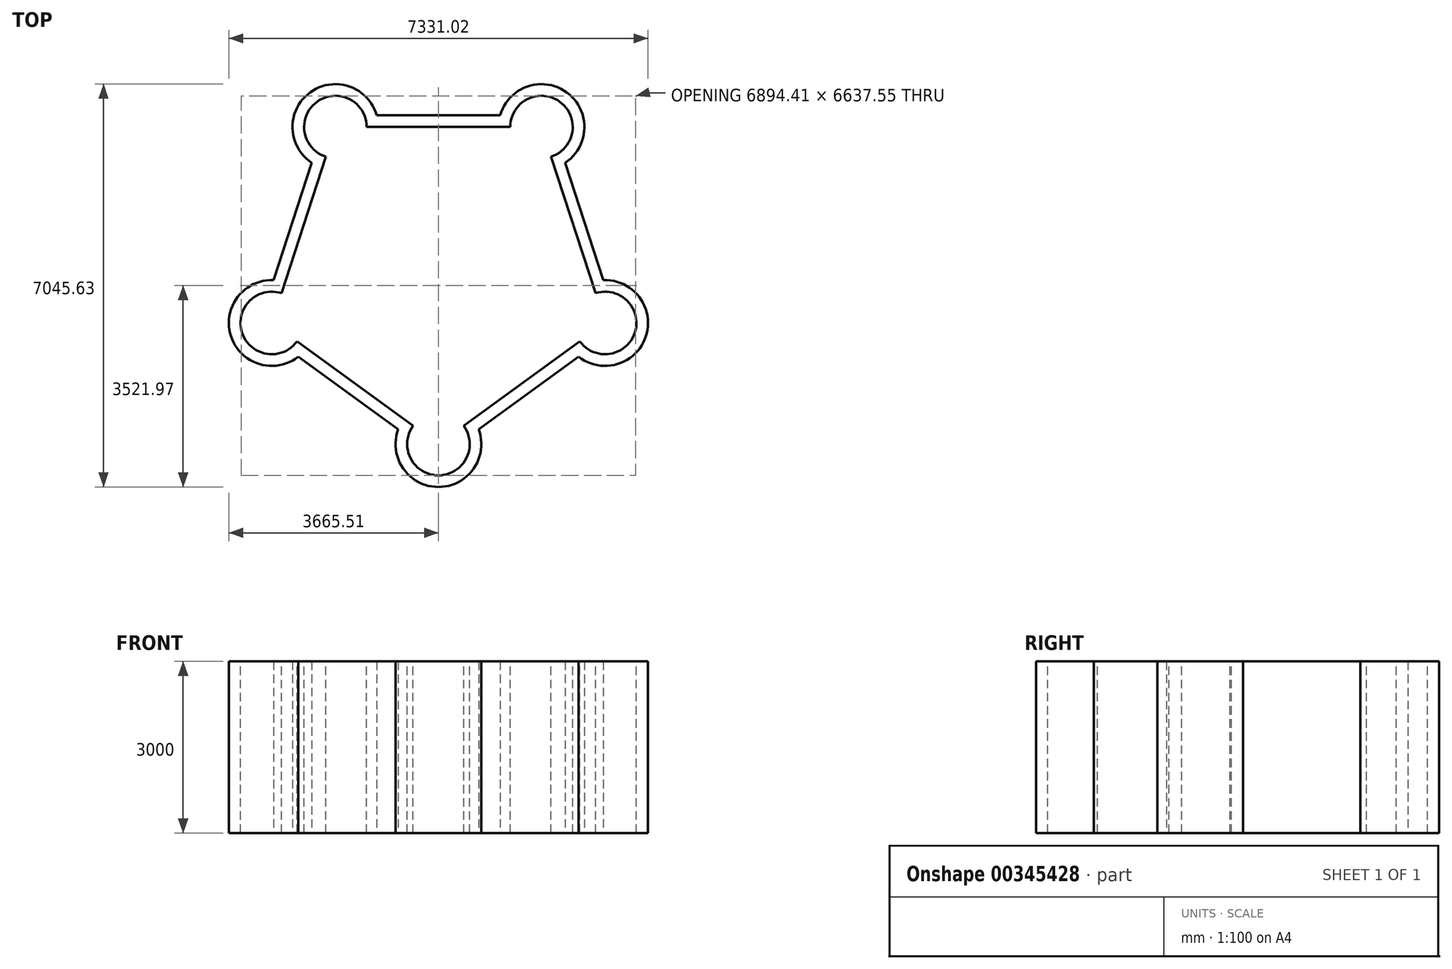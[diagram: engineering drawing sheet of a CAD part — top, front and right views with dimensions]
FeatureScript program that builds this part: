
annotation { "Feature Type Name" : "Feature", "Feature Type Description" : "" }
export const myFeature = defineFeature(function(context is Context, id is Id, definition is map)
    precondition{}
    {
        {
            var Q0;
            Q0=qCreatedBy(makeId("Top.planeOp"),FACE);
            var sketch = newSketch(context, id + "F0", { "sketchPlane" : qUnion([Q0])});
            skCircle(sketch, "E0.cCircle", {"center": v(0, 0) * mm, "radius": 2683.28 * mm, "construction": true});
            skLineSegment(sketch, "E0.0", {"start": v(-1949.52, 2683.28) * mm, "end": v(1949.52, 2683.28) * mm});
            skLineSegment(sketch, "E0.1", {"start": v(1949.52, 2683.28) * mm, "end": v(3154.39, -1024.92) * mm});
            skLineSegment(sketch, "E0.2", {"start": v(3154.39, -1024.92) * mm, "end": v(0, -3316.72) * mm});
            skLineSegment(sketch, "E0.3", {"start": v(0, -3316.72) * mm, "end": v(-3154.39, -1024.92) * mm});
            skLineSegment(sketch, "E0.4", {"start": v(-3154.39, -1024.92) * mm, "end": v(-1949.52, 2683.28) * mm});
            skPoint(sketch, "E0.0.midPoint", {"position": v(0, 2683.28) * mm});
            skCircle(sketch, "E1", {"center": v(-1801.88, 2480.08) * mm, "radius": 750 * mm});
            skCircle(sketch, "E2", {"center": v(1801.88, 2480.08) * mm, "radius": 750 * mm});
            skCircle(sketch, "E3", {"center": v(2915.51, -947.3) * mm, "radius": 750 * mm});
            skCircle(sketch, "E4", {"center": v(0, -3065.55) * mm, "radius": 750 * mm});
            skCircle(sketch, "E5", {"center": v(-2915.51, -947.3) * mm, "radius": 750 * mm});
            skSolve(sketch);
        }
        {
            var Q0;
            {var subQ13=sQuery(id+"F0.wireOp",EDGE,"E1");var subQ14=sQuery(id+"F0.wireOp",EDGE,"E0.0");var subQ15=makeQuery(id+"F0.imprint","INTERSECT",VERTEX,{"derivedFrom":[subQ14,subQ13]});Q0=makeQuery(id+"F0.imprint","IMPRINT",FACE,{"disambiguationData":[TD([[makeQuery(id+"F0.imprint","IMPRINT",EDGE,{"disambiguationData":[TD([[subQ15,-1.0]])],"derivedFrom":subQ14}),-1.0]])]});}
            var Q1;
            {var subQ0=sQuery(id+"F0.wireOp",EDGE,"E0.3");var subQ1=sQuery(id+"F0.wireOp",EDGE,"E0.2");var subQ2=makeQuery(id+"F0.imprint","INTERSECT",VERTEX,{"derivedFrom":[subQ1,subQ0]});Q1=makeQuery(id+"F0.imprint","IMPRINT",FACE,{"disambiguationData":[TD([[makeQuery(id+"F0.imprint","IMPRINT",EDGE,{"disambiguationData":[TD([[subQ2,1.0]])],"derivedFrom":subQ1}),1.0]])]});}
            var Q2;
            {var subQ0=sQuery(id+"F0.wireOp",EDGE,"E0.4");var subQ1=sQuery(id+"F0.wireOp",EDGE,"E0.3");var subQ2=makeQuery(id+"F0.imprint","INTERSECT",VERTEX,{"derivedFrom":[subQ1,subQ0]});Q2=makeQuery(id+"F0.imprint","IMPRINT",FACE,{"disambiguationData":[TD([[makeQuery(id+"F0.imprint","IMPRINT",EDGE,{"disambiguationData":[TD([[subQ2,1.0]])],"derivedFrom":subQ1}),1.0]])]});}
            var Q3;
            {var subQ0=sQuery(id+"F0.wireOp",EDGE,"E0.4");var subQ1=sQuery(id+"F0.wireOp",EDGE,"E0.3");var subQ2=makeQuery(id+"F0.imprint","INTERSECT",VERTEX,{"derivedFrom":[subQ1,subQ0]});Q3=makeQuery(id+"F0.imprint","IMPRINT",FACE,{"disambiguationData":[TD([[makeQuery(id+"F0.imprint","IMPRINT",EDGE,{"disambiguationData":[TD([[subQ2,1.0]])],"derivedFrom":subQ1}),-1.0]])]});}
            var Q4;
            {var subQ0=sQuery(id+"F0.wireOp",EDGE,"E0.4");var subQ1=sQuery(id+"F0.wireOp",EDGE,"E0.0");var subQ2=makeQuery(id+"F0.imprint","INTERSECT",VERTEX,{"derivedFrom":[subQ1,subQ0]});Q4=makeQuery(id+"F0.imprint","IMPRINT",FACE,{"disambiguationData":[TD([[makeQuery(id+"F0.imprint","IMPRINT",EDGE,{"disambiguationData":[TD([[subQ2,-1.0]])],"derivedFrom":subQ1}),-1.0]])]});}
            var Q5;
            {var subQ0=sQuery(id+"F0.wireOp",EDGE,"E0.4");var subQ1=sQuery(id+"F0.wireOp",EDGE,"E0.0");var subQ2=makeQuery(id+"F0.imprint","INTERSECT",VERTEX,{"derivedFrom":[subQ1,subQ0]});Q5=makeQuery(id+"F0.imprint","IMPRINT",FACE,{"disambiguationData":[TD([[makeQuery(id+"F0.imprint","IMPRINT",EDGE,{"disambiguationData":[TD([[subQ2,-1.0]])],"derivedFrom":subQ1}),1.0]])]});}
            var Q6;
            {var subQ0=sQuery(id+"F0.wireOp",EDGE,"E0.1");var subQ1=sQuery(id+"F0.wireOp",EDGE,"E0.0");var subQ2=makeQuery(id+"F0.imprint","INTERSECT",VERTEX,{"derivedFrom":[subQ1,subQ0]});Q6=makeQuery(id+"F0.imprint","IMPRINT",FACE,{"disambiguationData":[TD([[makeQuery(id+"F0.imprint","IMPRINT",EDGE,{"disambiguationData":[TD([[subQ2,1.0]])],"derivedFrom":subQ1}),-1.0]])]});}
            var Q7;
            {var subQ0=sQuery(id+"F0.wireOp",EDGE,"E0.1");var subQ1=sQuery(id+"F0.wireOp",EDGE,"E0.0");var subQ2=makeQuery(id+"F0.imprint","INTERSECT",VERTEX,{"derivedFrom":[subQ1,subQ0]});Q7=makeQuery(id+"F0.imprint","IMPRINT",FACE,{"disambiguationData":[TD([[makeQuery(id+"F0.imprint","IMPRINT",EDGE,{"disambiguationData":[TD([[subQ2,1.0]])],"derivedFrom":subQ1}),1.0]])]});}
            var Q8;
            {var subQ0=sQuery(id+"F0.wireOp",EDGE,"E0.2");var subQ1=sQuery(id+"F0.wireOp",EDGE,"E0.1");var subQ2=makeQuery(id+"F0.imprint","INTERSECT",VERTEX,{"derivedFrom":[subQ1,subQ0]});Q8=makeQuery(id+"F0.imprint","IMPRINT",FACE,{"disambiguationData":[TD([[makeQuery(id+"F0.imprint","IMPRINT",EDGE,{"disambiguationData":[TD([[subQ2,1.0]])],"derivedFrom":subQ1}),-1.0]])]});}
            var Q9;
            {var subQ0=sQuery(id+"F0.wireOp",EDGE,"E0.2");var subQ1=sQuery(id+"F0.wireOp",EDGE,"E0.1");var subQ2=makeQuery(id+"F0.imprint","INTERSECT",VERTEX,{"derivedFrom":[subQ1,subQ0]});Q9=makeQuery(id+"F0.imprint","IMPRINT",FACE,{"disambiguationData":[TD([[makeQuery(id+"F0.imprint","IMPRINT",EDGE,{"disambiguationData":[TD([[subQ2,1.0]])],"derivedFrom":subQ1}),1.0]])]});}
            var Q10;
            {var subQ0=sQuery(id+"F0.wireOp",EDGE,"E0.3");var subQ1=sQuery(id+"F0.wireOp",EDGE,"E0.2");var subQ2=makeQuery(id+"F0.imprint","INTERSECT",VERTEX,{"derivedFrom":[subQ1,subQ0]});Q10=makeQuery(id+"F0.imprint","IMPRINT",FACE,{"disambiguationData":[TD([[makeQuery(id+"F0.imprint","IMPRINT",EDGE,{"disambiguationData":[TD([[subQ2,1.0]])],"derivedFrom":subQ1}),-1.0]])]});}
            extrude(context, id + "F1", {"entities" : qUnion([Q0, Q1, Q2, Q3, Q4, Q5, Q6, Q7, Q8, Q9, Q10]), "depth" : 3000 * mm});
        }
        {
            var Q0;
            Q0=makeQuery(id+"F1.opExtrude","CAP_FACE",FACE,{"disambiguationData":[OSD([sQuery(id+"F0.wireOp",EDGE,"E0.0"),sQuery(id+"F0.wireOp",EDGE,"E0.1"),sQuery(id+"F0.wireOp",EDGE,"E0.2"),sQuery(id+"F0.wireOp",EDGE,"E0.3"),sQuery(id+"F0.wireOp",EDGE,"E0.4"),sQuery(id+"F0.wireOp",EDGE,"E1"),sQuery(id+"F0.wireOp",EDGE,"E2"),sQuery(id+"F0.wireOp",EDGE,"E3"),sQuery(id+"F0.wireOp",EDGE,"E4"),sQuery(id+"F0.wireOp",EDGE,"E5")])],"isStart":false});
            var sketch = newSketch(context, id + "F2", { "sketchPlane" : qUnion([Q0])});
            skLineSegment(sketch, "E6.0.0", {"start": v(-2218.23, 1856.26) * mm, "end": v(-2885.67, -197.9) * mm});
            skArc(sketch, "E6.0.1", {"start": v(-2885.67, -197.9) * mm, "mid": v(-3628.8, -1179.07) * mm, "end": v(-2450.88, -1536.05) * mm});
            skLineSegment(sketch, "E6.0.2", {"start": v(-2450.88, -1536.05) * mm, "end": v(-703.5, -2805.6) * mm});
            skArc(sketch, "E6.0.3", {"start": v(-703.5, -2805.6) * mm, "mid": v(0, -3815.55) * mm, "end": v(703.5, -2805.6) * mm});
            skLineSegment(sketch, "E6.0.4", {"start": v(703.5, -2805.6) * mm, "end": v(2450.88, -1536.05) * mm});
            skArc(sketch, "E6.0.5", {"start": v(2450.88, -1536.05) * mm, "mid": v(3628.8, -1179.07) * mm, "end": v(2885.67, -197.9) * mm});
            skLineSegment(sketch, "E6.0.6", {"start": v(2885.67, -197.9) * mm, "end": v(2218.23, 1856.26) * mm});
            skArc(sketch, "E6.0.7", {"start": v(2218.23, 1856.26) * mm, "mid": v(2242.72, 3086.84) * mm, "end": v(1079.94, 2683.28) * mm});
            skLineSegment(sketch, "E6.0.8", {"start": v(1079.94, 2683.28) * mm, "end": v(-1079.94, 2683.28) * mm});
            skArc(sketch, "E6.0.9", {"start": v(-1079.94, 2683.28) * mm, "mid": v(-2242.72, 3086.84) * mm, "end": v(-2218.23, 1856.26) * mm});
            skArc(sketch, "E7.0", {"start": v(1970.86, 1960.04) * mm, "mid": v(2123.29, 2922.45) * mm, "end": v(1255.08, 2480.08) * mm});
            skLineSegment(sketch, "E7.1", {"start": v(2746.54, -427.27) * mm, "end": v(1970.86, 1960.04) * mm});
            skLineSegment(sketch, "E7.2", {"start": v(1255.08, 2480.08) * mm, "end": v(-1255.08, 2480.08) * mm});
            skArc(sketch, "E7.3", {"start": v(2473.14, -1268.7) * mm, "mid": v(3435.55, -1116.28) * mm, "end": v(2746.54, -427.27) * mm});
            skLineSegment(sketch, "E7.4", {"start": v(442.37, -2744.15) * mm, "end": v(2473.14, -1268.7) * mm});
            skArc(sketch, "E7.5", {"start": v(-442.37, -2744.15) * mm, "mid": v(0, -3612.35) * mm, "end": v(442.37, -2744.15) * mm});
            skArc(sketch, "E7.6", {"start": v(-1255.08, 2480.08) * mm, "mid": v(-2123.29, 2922.45) * mm, "end": v(-1970.86, 1960.04) * mm});
            skLineSegment(sketch, "E7.7", {"start": v(-1970.86, 1960.04) * mm, "end": v(-2746.54, -427.27) * mm});
            skArc(sketch, "E7.8", {"start": v(-2746.54, -427.27) * mm, "mid": v(-3435.55, -1116.28) * mm, "end": v(-2473.14, -1268.7) * mm});
            skLineSegment(sketch, "E7.9", {"start": v(-2473.14, -1268.7) * mm, "end": v(-442.37, -2744.15) * mm});
            skLineSegment(sketch, "E8.bottom", {"start": v(-500, 2683.28) * mm, "end": v(500, 2683.28) * mm});
            skLineSegment(sketch, "E8.top", {"start": v(-500, 2480.08) * mm, "end": v(500, 2480.08) * mm});
            skLineSegment(sketch, "E8.left", {"start": v(-500, 2683.28) * mm, "end": v(-500, 2480.08) * mm});
            skLineSegment(sketch, "E8.right", {"start": v(500, 2683.28) * mm, "end": v(500, 2480.08) * mm});
            skLineSegment(sketch, "E9", {"start": v(0, 0) * mm, "end": v(0, 3119.03) * mm, "construction": true});
            skSolve(sketch);
        }
        {
            var Q0;
            Q0=makeQuery(id+"F2.imprint","IMPRINT",FACE,{"disambiguationData":[TD([[makeQuery(id+"F2.imprint","IMPRINT",EDGE,{"derivedFrom":sQuery(id+"F2.wireOp",EDGE,"E7.0")}),1.0]])]});
            var Q1;
            Q1=makeQuery(id+"F2.imprint","IMPRINT",FACE,{"disambiguationData":[TD([[makeQuery(id+"F2.imprint","IMPRINT",EDGE,{"derivedFrom":sQuery(id+"F2.wireOp",EDGE,"E8.bottom")}),-1.0]])]});
            extrude(context, id + "F3", {"entities" : qUnion([Q0, Q1]), "operationType" : NewBodyOperationType.REMOVE, "oppositeDirection" : true, "depth" : 3000 * mm});
        }
    });
